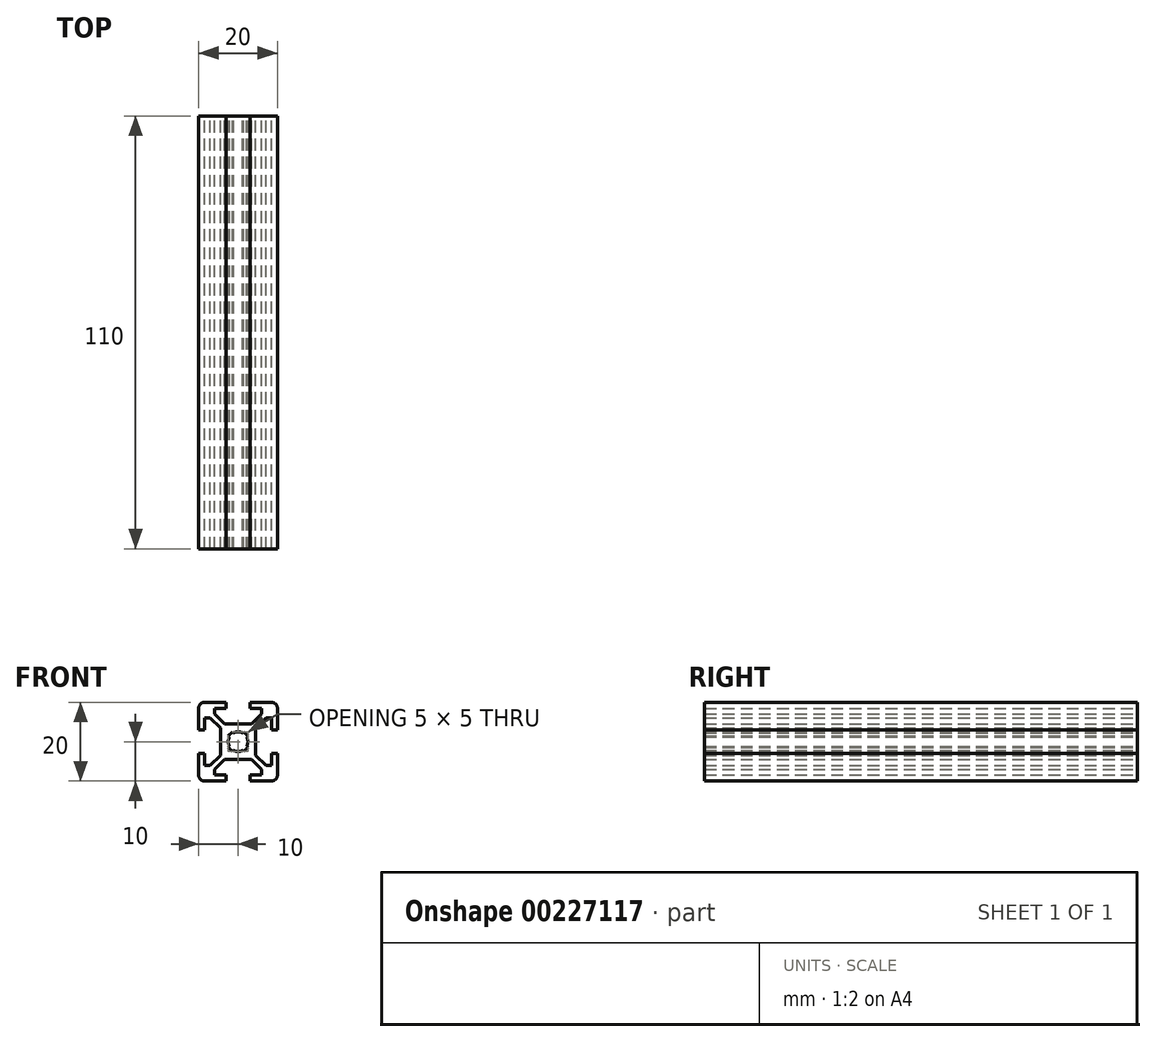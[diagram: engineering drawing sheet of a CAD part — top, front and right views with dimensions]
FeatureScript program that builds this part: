
annotation { "Feature Type Name" : "Feature", "Feature Type Description" : "" }
export const myFeature = defineFeature(function(context is Context, id is Id, definition is map)
    precondition{}
    {
        {
            var Q0;
            Q0=qCreatedBy(makeId("Front.planeOp"),FACE);
            var sketch = newSketch(context, id + "F0", { "sketchPlane" : qUnion([Q0])});
            skLineSegment(sketch, "E0.bottom", {"start": v(8.5, -10) * mm, "end": v(3, -10) * mm});
            skLineSegment(sketch, "E0.top", {"start": v(8.5, 10) * mm, "end": v(3, 10) * mm});
            skLineSegment(sketch, "E0.left", {"start": v(10, -8.5) * mm, "end": v(10, -3) * mm});
            skLineSegment(sketch, "E0.right", {"start": v(-10, -8.5) * mm, "end": v(-10, -3) * mm});
            skPoint(sketch, "E0.middle", {"position": v(0, 0) * mm});
            skLineSegment(sketch, "E1.bottom", {"start": v(6, -8.5) * mm, "end": v(3, -8.5) * mm});
            skLineSegment(sketch, "E1.top", {"start": v(6, 8.5) * mm, "end": v(3, 8.5) * mm});
            skLineSegment(sketch, "E1.left", {"start": v(8.5, -6) * mm, "end": v(8.5, -3) * mm});
            skLineSegment(sketch, "E1.right", {"start": v(-8.5, -6) * mm, "end": v(-8.5, -3) * mm});
            skLineSegment(sketch, "E2.bottom", {"start": v(3.44, -4.5) * mm, "end": v(-3.44, -4.5) * mm});
            skLineSegment(sketch, "E2.top", {"start": v(3.44, 4.5) * mm, "end": v(-3.44, 4.5) * mm});
            skLineSegment(sketch, "E2.left", {"start": v(4.5, -3.44) * mm, "end": v(4.5, 3.44) * mm});
            skLineSegment(sketch, "E2.right", {"start": v(-4.5, -3.44) * mm, "end": v(-4.5, 3.44) * mm});
            skLineSegment(sketch, "E3.bottom", {"start": v(8.5, -6) * mm, "end": v(7.06, -6) * mm});
            skLineSegment(sketch, "E3.top", {"start": v(8.5, 6) * mm, "end": v(7.06, 6) * mm});
            skLineSegment(sketch, "E4.left", {"start": v(6, -8.5) * mm, "end": v(6, -7.06) * mm});
            skLineSegment(sketch, "E4.right", {"start": v(-6, -8.5) * mm, "end": v(-6, -7.06) * mm});
            skPoint(sketch, "E5.orphan", {"position": v(-8.5, 8.5) * mm});
            skPoint(sketch, "E6.orphan", {"position": v(8.5, 8.5) * mm});
            skPoint(sketch, "E7.orphan", {"position": v(8.5, -8.5) * mm});
            skPoint(sketch, "E8.orphan", {"position": v(-8.5, -8.5) * mm});
            skLineSegment(sketch, "E9.trimOffspring", {"start": v(-6, 7.06) * mm, "end": v(-6, 8.5) * mm});
            skLineSegment(sketch, "E10.trimOffspring", {"start": v(-7.06, 6) * mm, "end": v(-8.5, 6) * mm});
            skLineSegment(sketch, "E11.trimOffspring", {"start": v(6, 7.06) * mm, "end": v(6, 8.5) * mm});
            skLineSegment(sketch, "E12.trimOffspring", {"start": v(-7.06, -6) * mm, "end": v(-8.5, -6) * mm});
            skLineSegment(sketch, "E13", {"start": v(-10, 10) * mm, "end": v(0, 0) * mm, "construction": true});
            skLineSegment(sketch, "E14", {"start": v(10, 10) * mm, "end": v(0, 0) * mm, "construction": true});
            skLineSegment(sketch, "E15", {"start": v(-6, 7.06) * mm, "end": v(-3.44, 4.5) * mm});
            skPoint(sketch, "E15.endSnap0", {"position": v(7.25, -6) * mm});
            skLineSegment(sketch, "E16", {"start": v(6, -7.06) * mm, "end": v(3.44, -4.5) * mm});
            skLineSegment(sketch, "E17", {"start": v(7.06, 6) * mm, "end": v(4.5, 3.44) * mm});
            skLineSegment(sketch, "E18", {"start": v(6, 7.06) * mm, "end": v(3.44, 4.5) * mm});
            skPoint(sketch, "E19.orphan", {"position": v(6, -6) * mm});
            skPoint(sketch, "E20.orphan", {"position": v(-4.5, -4.5) * mm});
            skPoint(sketch, "E21.orphan", {"position": v(-4.5, 4.5) * mm});
            skPoint(sketch, "E22.orphan", {"position": v(4.5, 4.5) * mm});
            skPoint(sketch, "E23.orphan", {"position": v(4.5, -4.5) * mm});
            skLineSegment(sketch, "E24.trimOffspring", {"start": v(4.5, -3.44) * mm, "end": v(7.06, -6) * mm});
            skLineSegment(sketch, "E25.trimOffspring", {"start": v(-3.44, -4.5) * mm, "end": v(-6, -7.06) * mm});
            skLineSegment(sketch, "E26.trimOffspring", {"start": v(-4.5, -3.44) * mm, "end": v(-7.06, -6) * mm});
            skLineSegment(sketch, "E27.trimOffspring", {"start": v(-4.5, 3.44) * mm, "end": v(-7.06, 6) * mm});
            skLineSegment(sketch, "E28.bottom", {"start": v(8.5, -3) * mm, "end": v(10, -3) * mm});
            skLineSegment(sketch, "E28.top", {"start": v(8.5, 3) * mm, "end": v(10, 3) * mm});
            skPoint(sketch, "E28.middle", {"position": v(10, 0) * mm});
            skLineSegment(sketch, "E29.left", {"start": v(3, 8.5) * mm, "end": v(3, 10) * mm});
            skLineSegment(sketch, "E29.right", {"start": v(-3, 8.5) * mm, "end": v(-3, 10) * mm});
            skPoint(sketch, "E29.middle", {"position": v(0, 10) * mm});
            skLineSegment(sketch, "E30.bottom", {"start": v(-8.5, 3) * mm, "end": v(-10, 3) * mm});
            skLineSegment(sketch, "E30.top", {"start": v(-8.5, -3) * mm, "end": v(-10, -3) * mm});
            skPoint(sketch, "E30.middle", {"position": v(-10, 0) * mm});
            skLineSegment(sketch, "E31.left", {"start": v(3, -8.5) * mm, "end": v(3, -10) * mm});
            skLineSegment(sketch, "E31.right", {"start": v(-3, -8.5) * mm, "end": v(-3, -10) * mm});
            skPoint(sketch, "E31.middle", {"position": v(0, -10) * mm});
            skPoint(sketch, "E32.orphan", {"position": v(3, 11.5) * mm});
            skPoint(sketch, "E33.orphan", {"position": v(-3, 11.5) * mm});
            skLineSegment(sketch, "E34.trimOffspring", {"start": v(-3, 10) * mm, "end": v(-8.5, 10) * mm});
            skLineSegment(sketch, "E35.trimOffspring", {"start": v(-3, 8.5) * mm, "end": v(-6, 8.5) * mm});
            skPoint(sketch, "E28.right.end.orphan", {"position": v(11.5, 3) * mm});
            skPoint(sketch, "E36.orphan", {"position": v(11.5, -3) * mm});
            skLineSegment(sketch, "E37.trimOffspring", {"start": v(10, 3) * mm, "end": v(10, 8.5) * mm});
            skLineSegment(sketch, "E38.trimOffspring", {"start": v(8.5, 3) * mm, "end": v(8.5, 6) * mm});
            skPoint(sketch, "E39.orphan", {"position": v(3, -11.5) * mm});
            skPoint(sketch, "E40.orphan", {"position": v(-3, -11.5) * mm});
            skLineSegment(sketch, "E41.trimOffspring", {"start": v(-3, -10) * mm, "end": v(-8.5, -10) * mm});
            skLineSegment(sketch, "E42.trimOffspring", {"start": v(-3, -8.5) * mm, "end": v(-6, -8.5) * mm});
            skPoint(sketch, "E30.right.end.orphan", {"position": v(-11.5, -3) * mm});
            skPoint(sketch, "E43.orphan", {"position": v(-11.5, 3) * mm});
            skLineSegment(sketch, "E44.trimOffspring", {"start": v(-10, 3) * mm, "end": v(-10, 8.5) * mm});
            skLineSegment(sketch, "E45.trimOffspring", {"start": v(-8.5, 3) * mm, "end": v(-8.5, 6) * mm});
            skLineSegment(sketch, "E46.trimOffspring", {"start": v(0, 0) * mm, "end": v(10, -10) * mm, "construction": true});
            skLineSegment(sketch, "E47.trimOffspring", {"start": v(0, 0) * mm, "end": v(-10, -10) * mm, "construction": true});
            skArc(sketch, "E48", {"start": v(1.16, 2.22) * mm, "mid": v(0, 2.5) * mm, "end": v(-1.16, 2.22) * mm});
            skLineSegment(sketch, "E49", {"start": v(-2.5, -1.44) * mm, "end": v(1.44, 2.5) * mm});
            skLineSegment(sketch, "E50", {"start": v(2.5, 1.44) * mm, "end": v(-1.44, -2.5) * mm});
            skLineSegment(sketch, "E51", {"start": v(1.44, -2.5) * mm, "end": v(-2.5, 1.44) * mm});
            skLineSegment(sketch, "E52", {"start": v(-1.44, 2.5) * mm, "end": v(2.5, -1.44) * mm});
            skLineSegment(sketch, "E53", {"start": v(2.5, 1.44) * mm, "end": v(2.5, -1.44) * mm, "construction": true});
            skLineSegment(sketch, "E54", {"start": v(1.44, -2.5) * mm, "end": v(-1.44, -2.5) * mm, "construction": true});
            skLineSegment(sketch, "E55", {"start": v(-2.5, -1.44) * mm, "end": v(-2.5, 1.44) * mm, "construction": true});
            skLineSegment(sketch, "E56", {"start": v(-1.44, 2.5) * mm, "end": v(1.44, 2.5) * mm, "construction": true});
            skLineSegment(sketch, "E57", {"start": v(-1.44, 2.5) * mm, "end": v(-2.5, 1.44) * mm});
            skLineSegment(sketch, "E58", {"start": v(1.44, 2.5) * mm, "end": v(2.5, 1.44) * mm});
            skLineSegment(sketch, "E59", {"start": v(2.5, -1.44) * mm, "end": v(1.44, -2.5) * mm});
            skLineSegment(sketch, "E60", {"start": v(-1.44, -2.5) * mm, "end": v(-2.5, -1.44) * mm});
            skArc(sketch, "E61.trimOffspring", {"start": v(-2.22, 1.16) * mm, "mid": v(-2.5, 0) * mm, "end": v(-2.22, -1.16) * mm});
            skArc(sketch, "E62.trimOffspring", {"start": v(-1.16, -2.22) * mm, "mid": v(0, -2.5) * mm, "end": v(1.16, -2.22) * mm});
            skArc(sketch, "E63.trimOffspring", {"start": v(2.22, -1.16) * mm, "mid": v(2.5, 0) * mm, "end": v(2.22, 1.16) * mm});
            skPoint(sketch, "E64.visualSharp", {"position": v(10, 10) * mm});
            skArc(sketch, "E64.filletArc", {"start": v(10, 8.5) * mm, "mid": v(9.56, 9.56) * mm, "end": v(8.5, 10) * mm});
            skPoint(sketch, "E65.visualSharp", {"position": v(10, -10) * mm});
            skArc(sketch, "E65.filletArc", {"start": v(8.5, -10) * mm, "mid": v(9.56, -9.56) * mm, "end": v(10, -8.5) * mm});
            skPoint(sketch, "E66.visualSharp", {"position": v(-10, -10) * mm});
            skArc(sketch, "E66.filletArc", {"start": v(-10, -8.5) * mm, "mid": v(-9.56, -9.56) * mm, "end": v(-8.5, -10) * mm});
            skPoint(sketch, "E67.visualSharp", {"position": v(-10, 10) * mm});
            skArc(sketch, "E67.filletArc", {"start": v(-8.5, 10) * mm, "mid": v(-9.56, 9.56) * mm, "end": v(-10, 8.5) * mm});
            skSolve(sketch);
        }
        {
            assignVariable(context, id + "F2", {"name" : "Length", "anyValue" : 110});
        }
        {
            var Q0;
            Q0=qSketchRegion(id+"F0",true);
            extrude(context, id + "F1", {"entities" : qUnion([Q0]), "depth" : (getVariable(context, 'Length')) * mm});
        }
    });
